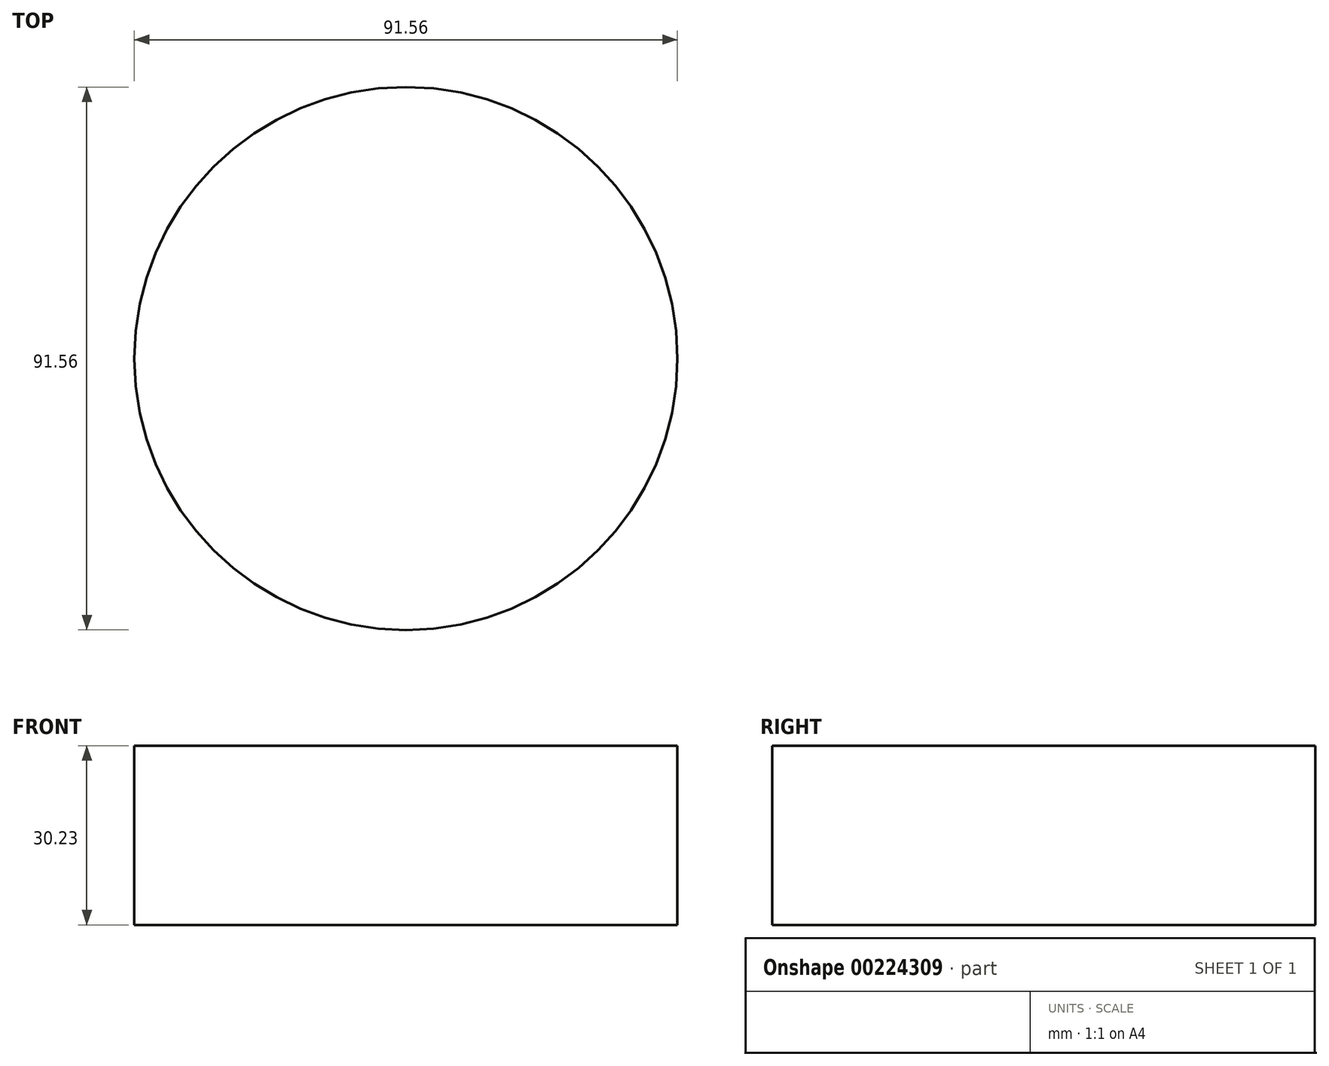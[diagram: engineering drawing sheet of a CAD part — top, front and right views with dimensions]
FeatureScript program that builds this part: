
annotation { "Feature Type Name" : "Feature", "Feature Type Description" : "" }
export const myFeature = defineFeature(function(context is Context, id is Id, definition is map)
    precondition{}
    {
        {
            var Q0;
            Q0=qCreatedBy(makeId("Top.planeOp"),FACE);
            var sketch = newSketch(context, id + "F0", { "sketchPlane" : qUnion([Q0])});
            skCircle(sketch, "E0", {"center": v(0, 0) * mm, "radius": 45.78 * mm});
            skSolve(sketch);
        }
        {
            var Q0;
            Q0=makeQuery(id+"F0.imprint","IMPRINT",FACE,{"disambiguationData":[TD([[makeQuery(id+"F0.imprint","IMPRINT",EDGE,{"derivedFrom":sQuery(id+"F0.wireOp",EDGE,"E0")}),1.0]])]});
            extrude(context, id + "F1", {"entities" : qUnion([Q0]), "depth" : 30.23 * mm});
        }
    });
